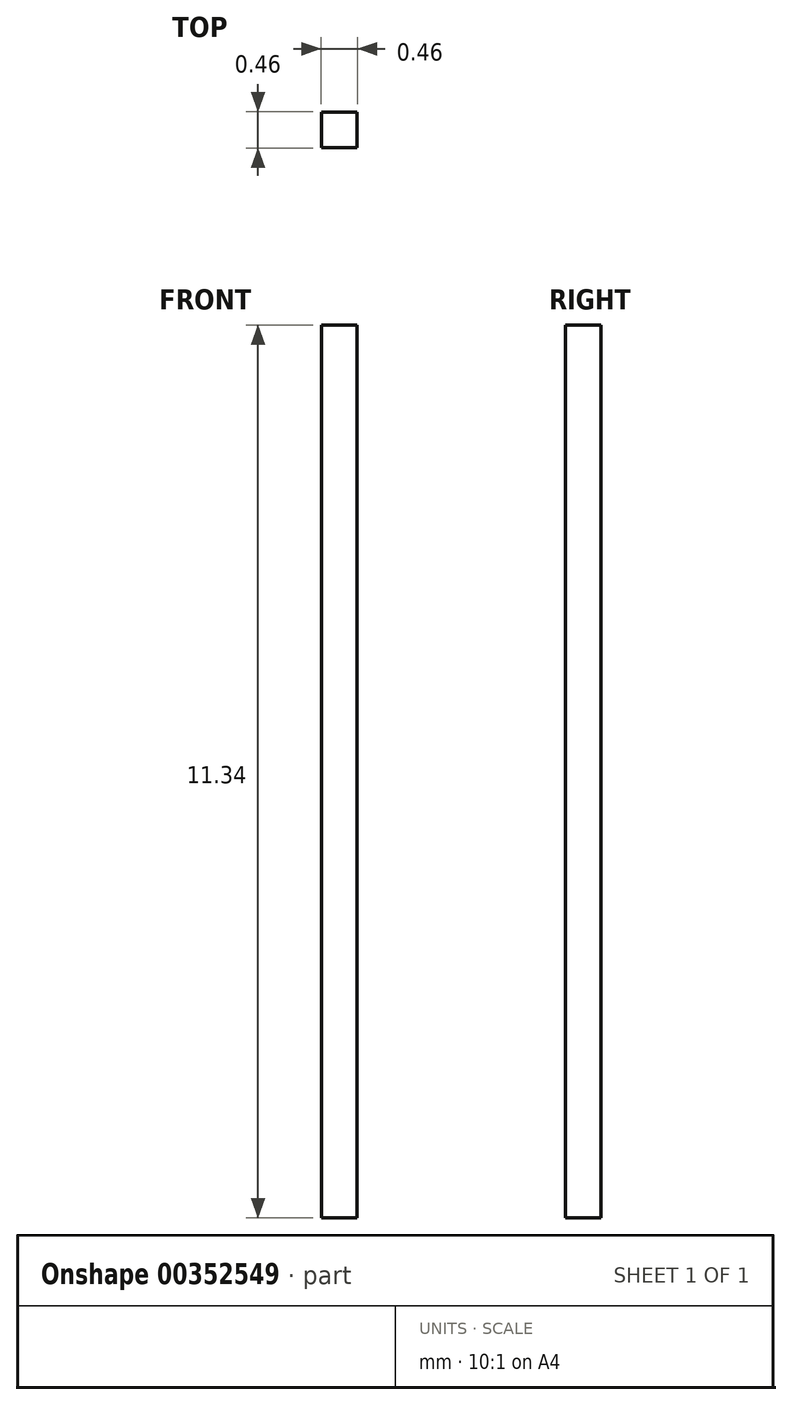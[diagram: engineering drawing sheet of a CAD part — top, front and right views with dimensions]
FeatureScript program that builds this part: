
annotation { "Feature Type Name" : "Feature", "Feature Type Description" : "" }
export const myFeature = defineFeature(function(context is Context, id is Id, definition is map)
    precondition{}
    {
        {
            var Q0;
            Q0=qCreatedBy(makeId("Top.planeOp"),FACE);
            var sketch = newSketch(context, id + "F0", { "sketchPlane" : qUnion([Q0])});
            skLineSegment(sketch, "E0.bottom", {"start": v(0.23, 0.23) * mm, "end": v(-0.23, 0.23) * mm});
            skLineSegment(sketch, "E0.top", {"start": v(0.23, -0.23) * mm, "end": v(-0.23, -0.23) * mm});
            skLineSegment(sketch, "E0.left", {"start": v(0.23, 0.23) * mm, "end": v(0.23, -0.23) * mm});
            skLineSegment(sketch, "E0.right", {"start": v(-0.23, 0.23) * mm, "end": v(-0.23, -0.23) * mm});
            skPoint(sketch, "E0.middle", {"position": v(0, 0) * mm});
            skSolve(sketch);
        }
        {
            var Q0;
            Q0 = qSketchRegion(id + "F0", true);
            extrude(context, id + "F1", {"entities" : qUnion([Q0]), "endBound" : BoundingType.SYMMETRIC, "depth" : 11.34 * mm});
        }
    });
